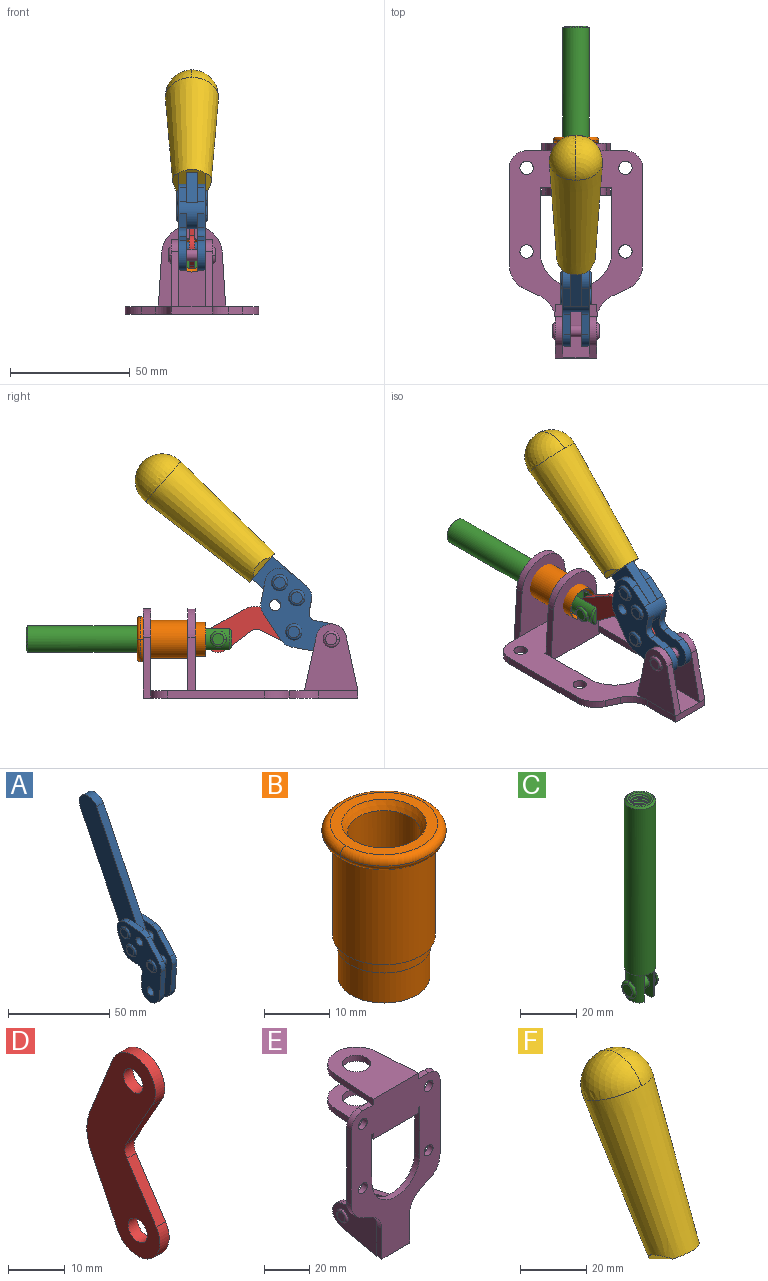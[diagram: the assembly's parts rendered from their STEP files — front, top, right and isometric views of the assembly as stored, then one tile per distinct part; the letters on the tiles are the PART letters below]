
ASSEMBLY  parts=6 mates=6
PART A: 59 faces, bbox 12.9x60.2x99.6 mm
  f0: torus R=2.39mm, axis (-1,0,0), area 14.9mm2, adj f20,f43,f51
  f1: torus R=2.39mm, axis (-1,0,0), area 14.9mm2, adj f19,f42,f51
  f2: torus R=2.39mm, axis (-1,0,0), area 14.9mm2, adj f18,f35,f51
  f3: torus R=2.39mm, axis (-1,0,0), area 14.9mm2, adj f14,f17,f23
  f4: torus R=2.39mm, axis (-1,0,0), area 14.9mm2, adj f13,f16,f23
  f5: torus R=2.39mm, axis (-1,0,0), area 14.9mm2, adj f12,f15,f23
  f6: cylinder r=2.39mm len=4.78mm, axis (1,0,0), area 46.5mm2, adj f48,f50,f51
  f7: cylinder r=2.39mm len=4.78mm, axis (1,0,0), area 46.5mm2, adj f50,f51
  f8: cylinder r=6.35mm len=12.68mm, axis (1,0,0), area 61.8mm2, adj f38,f39,f50,f51
  f9: cylinder r=2.39mm len=4.78mm, axis (-1,0,0), area 70.5mm2, adj f46,f50
  f10: cylinder r=2.39mm len=4.78mm, axis (-1,0,0), area 46.5mm2, adj f23,f45,f46
  f11: cylinder r=2.39mm len=4.78mm, axis (-1,0,0), area 46.5mm2, adj f23,f46
  f12: plane 4.78x4.78mm, normal (1,0,0), area 17.9mm2, adj f5,f15
  f13: plane 4.78x4.78mm, normal (1,0,0), area 17.9mm2, adj f4,f16
  f14: plane 4.78x4.78mm, normal (1,0,0), area 17.9mm2, adj f3,f17
  f15: torus R=2.39mm, axis (-1,0,0), area 14.9mm2, adj f5,f12,f23
  f16: torus R=2.39mm, axis (-1,0,0), area 14.9mm2, adj f4,f13,f23
  f17: torus R=2.39mm, axis (-1,0,0), area 14.9mm2, adj f3,f14,f23
  f18: plane 4.78x4.78mm, normal (-1,0,0), area 17.9mm2, adj f2,f35
  f19: plane 4.78x4.78mm, normal (-1,0,0), area 17.9mm2, adj f1,f42
  f20: plane 4.78x4.78mm, normal (-1,0,0), area 17.9mm2, adj f0,f43
  f21: plane 2.26x0.2mm, normal (1,0,0), area 0.2mm2, adj f31,f44
  f22: plane 2.26x0.2mm, normal (-1,0,0), area 0.2mm2, adj f41,f44
  f23: plane 39.37x30.77mm, normal (1,0,0), area 565.5mm2, adj f3,f4,f5,f10,f11,f15,f16,f17
  f24: cylinder r=6.1mm len=4.15mm, axis (-1,0,0), area 14.7mm2, adj f23,f25,f32,f46
  f25: plane 10.25x9.01mm, normal (0,-0.75,0.66), area 42.3mm2, adj f23,f24,f26,f46
  f26: cylinder r=6.35mm len=4.64mm, axis (-1,0,0), area 15.6mm2, adj f23,f25,f27,f46
  f27: plane 15.84x3.1mm, normal (0,-1,-0.07), area 49.2mm2, adj f23,f26,f28,f46
  f28: cylinder r=6.35mm len=12.68mm, axis (-1,0,0), area 61.8mm2, adj f23,f27,f29,f46
  f29: plane 8.11x3.1mm, normal (0,1,0.07), area 25.2mm2, adj f23,f28,f30,f46
  f30: cylinder r=3.05mm len=3.25mm, axis (-1,0,0), area 14.8mm2, adj f23,f29,f31,f46
  f31: plane 5.99x3.1mm, normal (0,0.07,-1), area 18.6mm2, adj f21,f23,f30,f44,f46
  f32: plane 9.5x3.1mm, normal (0,-0.07,1), area 29.5mm2, adj f23,f24,f33,f46,f47
  f33: cylinder r=6.1mm len=8.63mm, axis (-1,0,0), area 39.1mm2, adj f23,f32,f34,f47
  f34: plane 8.65x3.96mm, normal (0,0.91,-0.42), area 29.5mm2, adj f23,f33,f44,f47
  f35: torus R=2.39mm, axis (-1,0,0), area 14.9mm2, adj f2,f18,f51
  f36: plane 10.25x9.01mm, normal (0,-0.75,0.66), area 42.3mm2, adj f37,f49,f50,f51
  f37: cylinder r=6.35mm len=4.64mm, axis (1,0,0), area 15.6mm2, adj f36,f38,f50,f51
  f38: plane 15.84x3.1mm, normal (0,-1,-0.07), area 49.2mm2, adj f8,f37,f50,f51
  f39: plane 8.11x3.1mm, normal (0,1,0.07), area 25.2mm2, adj f8,f40,f50,f51
  f40: cylinder r=3.05mm len=3.25mm, axis (1,0,0), area 14.8mm2, adj f39,f41,f50,f51
  f41: plane 5.99x3.1mm, normal (0,0.07,-1), area 18.6mm2, adj f22,f40,f44,f50,f51
  f42: torus R=2.39mm, axis (-1,0,0), area 14.9mm2, adj f1,f19,f51
  f43: torus R=2.39mm, axis (-1,0,0), area 14.9mm2, adj f0,f20,f51
  f44: cylinder r=6.35mm len=12.12mm, axis (-1,0,0), area 128.9mm2, adj f21,f22,f23,f31,f34,f41,f46,f47
  f45: plane 2.65x1.35mm, normal (1,0,0), area 1mm2, adj f10,f55
  f46: plane 39.08x20.42mm, normal (-1,0,0), area 412.5mm2, adj f9,f10,f11,f24,f25,f26,f27,f28
  f47: plane 77.62x39.82mm, normal (1,0,0), area 850mm2, adj f32,f33,f34,f44,f53,f54,f55
  f48: plane 2.65x1.35mm, normal (-1,0,0), area 1mm2, adj f6,f55
  f49: cylinder r=6.1mm len=4.15mm, axis (1,0,0), area 14.7mm2, adj f36,f50,f51,f56
  f50: plane 39.08x20.42mm, normal (1,0,0), area 412.5mm2, adj f6,f7,f8,f9,f36,f37,f38,f39
  f51: plane 39.37x30.77mm, normal (-1,0,0), area 565.5mm2, adj f0,f1,f2,f6,f7,f8,f35,f36
  f52: plane 8.65x3.96mm, normal (0,0.91,-0.42), area 29.5mm2, adj f44,f51,f57,f58
  f53: plane 68.49x33.4mm, normal (0,0.9,-0.44), area 358.1mm2, adj f44,f47,f54,f58
  f54: cylinder r=6.35mm len=12.06mm, axis (1,0,0), area 93.7mm2, adj f47,f53,f55,f58
  f55: plane 68.49x33.4mm, normal (0,-0.9,0.44), area 358.1mm2, adj f44,f45,f46,f47,f48,f50,f54,f58
  f56: plane 9.5x3.1mm, normal (0,-0.07,1), area 29.5mm2, adj f49,f50,f51,f57,f58
  f57: cylinder r=6.1mm len=8.63mm, axis (1,0,0), area 39.1mm2, adj f51,f52,f56,f58
  f58: plane 77.62x39.82mm, normal (-1,0,0), area 850mm2, adj f44,f52,f53,f54,f55,f56,f57
PART B: 15 faces, bbox 20.6x20.6x28.7 mm
  f0: torus R=8.26mm, axis (0,0,1), area 56.8mm2, adj f1,f10,f12
  f1: torus R=8.26mm, axis (0,0,1), area 56.8mm2, adj f0,f6,f13
  f2: cylinder r=5.59mm len=25.91mm, axis (0,0,1), area 909.6mm2, adj f3,f4
  f3: cone r=6.86mm half-angle=45deg, axis (0,0,-1), area 70.2mm2, adj f2,f14
  f4: cone r=6.47mm half-angle=30deg, axis (0,0,1), area 66.7mm2, adj f2,f13
  f5: cylinder r=7.04mm len=14.07mm, axis (0,0,1), area 252.6mm2, adj f11,f14
  f6: torus R=8.26mm, axis (0,0,1), area 56.8mm2, adj f1,f12,f13
  f7: cylinder r=7.16mm len=14.33mm, axis (0,0,1), area 91.5mm2, adj f9,f11
  f8: cylinder r=7.86mm len=18.42mm, axis (0,0,1), area 909.6mm2, adj f9,f10
  f9: plane 15.72x15.72mm, normal (0,0,-1), area 33mm2, adj f7,f8
  f10: plane 16.51x16.51mm, normal (0,0,-1), area 19.9mm2, adj f0,f8,f12
  f11: plane 14.33x14.33mm, normal (0,0,-1), area 5.7mm2, adj f5,f7
  f12: torus R=8.26mm, axis (0,0,1), area 56.8mm2, adj f0,f6,f10
  f13: plane 16.51x16.51mm, normal (0,0,1), area 82.7mm2, adj f1,f4,f6
  f14: plane 14.07x14.07mm, normal (0,0,-1), area 7.8mm2, adj f3,f5
PART C: 48 faces, bbox 12.6x11.1x86.1 mm
  f0: torus R=2.41mm, axis (-1,0,0), area 15mm2, adj f30,f32,f34
  f1: torus R=2.41mm, axis (-1,0,0), area 15mm2, adj f29,f31,f33
  f2: cylinder r=5.54mm len=72.39mm, axis (0,0,1), area 2518.5mm2, adj f3,f4,f42,f43
  f3: cone r=5.54mm half-angle=45deg, axis (0,0,1), area 7.6mm2, adj f2,f5,f41
  f4: cone r=5.54mm half-angle=45deg, axis (0,0,-1), area 34.9mm2, adj f2,f39
  f5: cylinder r=5.08mm len=11.48mm, axis (0,0,1), area 108.3mm2, adj f3,f7,f8,f41
  f6: cylinder r=2.41mm len=4.83mm, axis (-1,0,0), area 71.2mm2, adj f40,f41
  f7: cylinder r=2.41mm len=4.83mm, axis (-1,0,0), area 7.6mm2, adj f5,f34
  f8: cone r=5.08mm half-angle=45deg, axis (0,0,1), area 10.6mm2, adj f5,f37,f41
  f9: cone r=3.98mm half-angle=45deg, axis (0,0,1), area 17.6mm2, adj f27,f39,f45,f46,f47
  f10: cylinder r=2.41mm len=4.83mm, axis (-1,0,0), area 7.6mm2, adj f33,f38
  f11: cylinder r=3.2mm len=6.4mm, axis (0,0,1), area 78.4mm2, adj f12,f28,f44,f45,f47
  f12: cylinder r=3.2mm len=6.4mm, axis (0,0,1), area 10.5mm2, adj f11,f13,f45,f47
  f13: cylinder r=3.2mm len=6.4mm, axis (0,0,1), area 10.5mm2, adj f12,f14,f45,f47
  f14: cylinder r=3.2mm len=6.4mm, axis (0,0,1), area 10.5mm2, adj f13,f15,f45,f47
  f15: cylinder r=3.2mm len=6.4mm, axis (0,0,1), area 10.5mm2, adj f14,f16,f45,f47
  f16: cylinder r=3.2mm len=6.4mm, axis (0,0,1), area 10.5mm2, adj f15,f17,f45,f47
  f17: cylinder r=3.2mm len=6.4mm, axis (0,0,1), area 10.5mm2, adj f16,f18,f45,f47
  f18: cylinder r=3.2mm len=6.4mm, axis (0,0,1), area 10.5mm2, adj f17,f19,f45,f47
  f19: cylinder r=3.2mm len=6.4mm, axis (0,0,1), area 10.5mm2, adj f18,f20,f45,f47
  f20: cylinder r=3.2mm len=6.4mm, axis (0,0,1), area 10.5mm2, adj f19,f21,f45,f47
  f21: cylinder r=3.2mm len=6.4mm, axis (0,0,1), area 10.5mm2, adj f20,f22,f45,f47
  f22: cylinder r=3.2mm len=6.4mm, axis (0,0,1), area 10.5mm2, adj f21,f23,f45,f47
  f23: cylinder r=3.2mm len=6.4mm, axis (0,0,1), area 10.5mm2, adj f22,f24,f45,f47
  f24: cylinder r=3.2mm len=6.4mm, axis (0,0,1), area 10.5mm2, adj f23,f25,f45,f47
  f25: cylinder r=3.2mm len=6.4mm, axis (0,0,1), area 10.5mm2, adj f24,f26,f45,f47
  f26: cylinder r=3.2mm len=6.4mm, axis (0,0,1), area 10.5mm2, adj f25,f27,f45,f47
  f27: cylinder r=3.2mm len=6.4mm, axis (0,0,1), area 7.4mm2, adj f9,f26,f45,f47
  f28: cone r=3.2mm half-angle=60deg, axis (0,0,1), area 37.2mm2, adj f11
  f29: plane 4.83x4.83mm, normal (-1,0,0), area 18.3mm2, adj f1,f31
  f30: plane 4.83x4.83mm, normal (1,0,0), area 18.3mm2, adj f0,f32
  f31: torus R=2.41mm, axis (-1,0,0), area 15mm2, adj f1,f29,f33
  f32: torus R=2.41mm, axis (-1,0,0), area 15mm2, adj f0,f30,f34
  f33: plane 6.83x6.83mm, normal (1,0,0), area 18.3mm2, adj f1,f10,f31
  f34: plane 6.83x6.83mm, normal (-1,0,0), area 18.3mm2, adj f0,f7,f32
  f35: cone r=5.08mm half-angle=45deg, axis (0,0,1), area 10.6mm2, adj f36,f38,f40
  f36: plane 7.25x1.97mm, normal (0,0,-1), area 10mm2, adj f35,f40
  f37: plane 7.25x1.97mm, normal (0,0,-1), area 10mm2, adj f8,f41
  f38: cylinder r=5.08mm len=11.48mm, axis (0,0,1), area 108.3mm2, adj f10,f35,f40,f42
  f39: plane 9.55x9.55mm, normal (0,0,1), area 22mm2, adj f4,f9
  f40: plane 12.76x10.09mm, normal (1,0,0), area 95.7mm2, adj f6,f35,f36,f38,f42,f43
  f41: plane 12.76x10.09mm, normal (-1,0,0), area 95.7mm2, adj f3,f5,f6,f8,f37,f43
  f42: cone r=5.54mm half-angle=45deg, axis (0,0,1), area 7.6mm2, adj f2,f38,f40
  f43: plane 11.07x4.7mm, normal (0,0,-1), area 50.4mm2, adj f2,f40,f41
  f44: plane 0.89x0.62mm, normal (-1,0,0), area 0.3mm2, adj f11,f45,f46,f47
  f45: bspline ~24.8x7.63mm, area 266.6mm2, adj f9,f11,f12,f13,f14,f15,f16,f17
  f46: bspline ~24.87x7.63mm, area 73.6mm2, adj f9,f44,f45,f47
  f47: bspline ~24.98x7.63mm, area 272.5mm2, adj f9,f11,f12,f13,f14,f15,f16,f17
PART D: 12 faces, bbox 2.3x18.2x42.8 mm
  f0: cylinder r=2.4mm len=4.8mm, axis (1,0,0), area 34.9mm2, adj f4,f11
  f1: cylinder r=10.41mm len=8.47mm, axis (1,0,0), area 20.2mm2, adj f4,f9,f10,f11
  f2: cylinder r=3.05mm len=3.16mm, axis (1,0,0), area 7.7mm2, adj f4,f6,f7,f11
  f3: cylinder r=2.4mm len=4.8mm, axis (1,0,0), area 34.9mm2, adj f4,f11
  f4: plane 42.81x18.23mm, normal (-1,0,0), area 414.1mm2, adj f0,f1,f2,f3,f5,f6,f7,f8
  f5: cylinder r=5.54mm len=10.67mm, axis (1,0,0), area 41.8mm2, adj f4,f6,f10,f11
  f6: plane 11.66x6.53mm, normal (0,-0.87,-0.49), area 30.9mm2, adj f2,f4,f5,f11
  f7: plane 11.17x7.33mm, normal (0,-0.84,0.55), area 30.9mm2, adj f2,f4,f8,f11
  f8: cylinder r=5.54mm len=10.51mm, axis (1,0,0), area 41.8mm2, adj f4,f7,f9,f11
  f9: plane 13.67x6.67mm, normal (0,0.9,-0.44), area 35.1mm2, adj f1,f4,f8,f11
  f10: plane 14.1x5.7mm, normal (0,0.93,0.37), area 35.1mm2, adj f1,f4,f5,f11
  f11: plane 42.81x18.23mm, normal (1,0,0), area 414.1mm2, adj f0,f1,f2,f3,f5,f6,f7,f8
PART E: 55 faces, bbox 55.7x37.4x89.8 mm
  f0: torus R=2.41mm, axis (-1,0,0), area 15mm2, adj f11,f15,f25
  f1: torus R=2.41mm, axis (-1,0,0), area 15mm2, adj f10,f12,f22
  f2: cylinder r=2.78mm len=5.56mm, axis (0,-1,0), area 54.2mm2, adj f30,f54
  f3: cylinder r=14.99mm len=29.97mm, axis (0,-1,0), area 145.9mm2, adj f30,f49,f53,f54
  f4: cylinder r=2.78mm len=5.56mm, axis (0,-1,0), area 54.2mm2, adj f30,f54
  f5: cylinder r=2.78mm len=5.56mm, axis (0,-1,0), area 54.2mm2, adj f30,f54
  f6: cylinder r=2.78mm len=5.56mm, axis (0,-1,0), area 54.2mm2, adj f30,f54
  f7: cylinder r=6.35mm len=12.7mm, axis (0,0,1), area 123.6mm2, adj f27,f51
  f8: cylinder r=6.35mm len=12.7mm, axis (0,0,-1), area 124.7mm2, adj f21,f35
  f9: cylinder r=2.41mm len=11.18mm, axis (-1,0,0), area 169.4mm2, adj f16,f19
  f10: plane 4.83x4.83mm, normal (1,0,0), area 18.3mm2, adj f1,f12
  f11: plane 4.83x4.83mm, normal (-1,0,0), area 18.3mm2, adj f0,f15
  f12: torus R=2.41mm, axis (-1,0,0), area 15mm2, adj f1,f10,f22
  f13: cylinder r=6.35mm len=12.41mm, axis (1,0,0), area 53.4mm2, adj f18,f19,f22,f23
  f14: cylinder r=6.35mm len=12.41mm, axis (-1,0,0), area 53.4mm2, adj f16,f17,f24,f25
  f15: torus R=2.41mm, axis (-1,0,0), area 15mm2, adj f0,f11,f25
  f16: plane 27.86x22.35mm, normal (1,0,0), area 425.4mm2, adj f9,f14,f17,f24,f30
  f17: plane 22.86x4.97mm, normal (0,0.21,0.98), area 72.5mm2, adj f14,f16,f25,f30
  f18: plane 22.86x4.97mm, normal (0,0.21,0.98), area 72.5mm2, adj f13,f19,f22,f30
  f19: plane 27.86x22.35mm, normal (-1,0,0), area 425.4mm2, adj f9,f13,f18,f23,f30
  f20: cylinder r=12.7mm len=25.35mm, axis (0,0,-1), area 119.8mm2, adj f21,f34,f35,f36
  f21: plane 34.21x28.07mm, normal (0,0,-1), area 702.4mm2, adj f8,f20,f30,f34,f36
  f22: plane 27.96x22.45mm, normal (1,0,0), area 407.2mm2, adj f1,f12,f13,f18,f23,f30,f42,f43
  f23: plane 22.86x4.97mm, normal (0,0.21,-0.98), area 72.5mm2, adj f13,f19,f22,f44
  f24: plane 22.86x4.97mm, normal (0,0.21,-0.98), area 72.5mm2, adj f14,f16,f25,f44
  f25: plane 27.86x22.35mm, normal (-1,0,0), area 407.1mm2, adj f0,f14,f15,f17,f24,f30,f45,f46
  f26: plane 3.1x0.95mm, normal (0,0,-1), area 2.7mm2, adj f30,f49,f50,f54
  f27: plane 34.21x28.07mm, normal (0,0,1), area 702.4mm2, adj f7,f28,f30,f50,f52
  f28: cylinder r=12.7mm len=25.35mm, axis (0,0,1), area 118.8mm2, adj f27,f50,f51,f52
  f29: plane 3.1x0.95mm, normal (0,0,-1), area 2.7mm2, adj f30,f52,f53,f54
  f30: plane 86.54x55.63mm, normal (0,1,0), area 2362.9mm2, adj f2,f3,f4,f5,f6,f16,f17,f18
  f31: plane 40.56x3.1mm, normal (-1,0,0), area 125.7mm2, adj f30,f32,f48,f54
  f32: cylinder r=7.11mm len=7.11mm, axis (0,-1,0), area 34.6mm2, adj f30,f31,f33,f54
  f33: plane 6.67x3.1mm, normal (0,0,1), area 20.4mm2, adj f30,f32,f34,f54
  f34: plane 25.39x3.13mm, normal (-1,0.06,0), area 79.5mm2, adj f20,f21,f33,f35,f54
  f35: plane 37.31x28.45mm, normal (0,0,1), area 789.9mm2, adj f8,f20,f34,f36,f54
  f36: plane 25.39x3.13mm, normal (1,0.06,0), area 79.5mm2, adj f20,f21,f35,f37,f54
  f37: plane 6.67x3.1mm, normal (0,0,1), area 20.4mm2, adj f30,f36,f38,f54
  f38: cylinder r=7.11mm len=7.11mm, axis (0,-1,0), area 34.6mm2, adj f30,f37,f39,f54
  f39: plane 40.56x3.1mm, normal (1,0,0), area 125.7mm2, adj f30,f38,f40,f54
  f40: cylinder r=11.18mm len=10.16mm, axis (0,-1,0), area 39.5mm2, adj f30,f39,f41,f54
  f41: plane 6.09x3.1mm, normal (0.42,0,-0.91), area 20.8mm2, adj f30,f40,f42,f54
  f42: cylinder r=11.18mm len=9.41mm, axis (0,-1,0), area 37.2mm2, adj f22,f30,f41,f43,f54
  f43: plane 16.5x3.1mm, normal (1,0,0), area 51.1mm2, adj f22,f42,f44,f54
  f44: plane 17.37x3.1mm, normal (0,0,-1), area 53.8mm2, adj f23,f24,f30,f43,f45,f54
  f45: plane 16.5x3.1mm, normal (-1,0,0), area 51.1mm2, adj f25,f44,f46,f54
  f46: cylinder r=11.18mm len=9.41mm, axis (0,-1,0), area 37.2mm2, adj f25,f30,f45,f47,f54
  f47: plane 6.09x3.1mm, normal (-0.42,0,-0.91), area 20.8mm2, adj f30,f46,f48,f54
  f48: cylinder r=11.18mm len=10.16mm, axis (0,-1,0), area 39.5mm2, adj f30,f31,f47,f54
  f49: plane 26.54x3.1mm, normal (-1,0,0), area 82.3mm2, adj f3,f26,f30,f54
  f50: plane 25.39x3.1mm, normal (1,0.06,0), area 78.8mm2, adj f26,f27,f28,f51,f54
  f51: plane 37.31x28.45mm, normal (0,0,-1), area 789.9mm2, adj f7,f28,f50,f52,f54
  f52: plane 25.39x3.1mm, normal (-1,0.06,0), area 78.8mm2, adj f27,f28,f29,f51,f54
  f53: plane 26.54x3.1mm, normal (1,0,0), area 82.3mm2, adj f3,f29,f30,f54
  f54: plane 89.66x55.63mm, normal (0,-1,0), area 2678.5mm2, adj f2,f3,f4,f5,f6,f26,f29,f31
PART F: 11 faces, bbox 22.3x42.6x64.5 mm
  f0: sphere r=11.13mm, area 411.4mm2, adj f1,f8
  f1: cone r=11.11mm half-angle=3.3deg, axis (0,0.44,0.9), area 3251.8mm2, adj f0,f7,f8,f9,f10
  f2: cylinder r=6.16mm len=11.7mm, axis (1,0,0), area 89.5mm2, adj f3,f4,f5,f6
  f3: plane 60.23x36.75mm, normal (-1,0,0), area 763.6mm2, adj f2,f4,f6,f10
  f4: plane 51.37x25.05mm, normal (0,0.9,-0.44), area 264.2mm2, adj f2,f3,f5,f10
  f5: plane 60.23x36.75mm, normal (1,0,0), area 763.6mm2, adj f2,f4,f6,f10
  f6: plane 51.37x25.05mm, normal (0,-0.9,0.44), area 264.2mm2, adj f2,f3,f5,f10
  f7: plane 9.95x5.95mm, normal (0.71,-0.31,-0.64), area 25.8mm2, adj f1,f10
  f8: sphere r=11.13mm, area 411.4mm2, adj f0,f1
  f9: plane 9.95x5.95mm, normal (-0.71,-0.31,-0.64), area 25.8mm2, adj f1,f10
  f10: plane 14.27x11.38mm, normal (0,-0.44,-0.9), area 106.7mm2, adj f1,f3,f4,f5,f6,f7,f9
PLACE A rot(axis=(0,-0.61,-0.79),180deg) t=(0,-3.86,9.14)mm
PLACE B rot(axis=(-1,0,0),90deg) t=(0,-9.14,49.23)mm
PLACE C rot(axis=(-1,0,0),90deg) t=(0,-9.52,49.23)mm
PLACE D rot(axis=(1,0,0),86.5deg) t=(0,-11.7,2.14)mm
PLACE E rot(axis=(0,-0.71,-0.71),180deg) t=(0,-9.14,0)mm fixed
PLACE F rot(axis=(0,0.61,0.79),180deg) t=(-0.04,-3.86,9.14)mm
MATE fastened F.f2 <-> A.f54  axis (1,0,0) through (-2.35,30.66,91.94)mm
MATE revolute D.f5 <-> A.f4  axis (1,0,0) through (0,-25.65,27.64)mm
MATE fastened B.f2 <-> E.f7  axis (0,1,0) through (0,37.25,24.61)mm
MATE revolute A.f7 <-> E.f0  axis (-1,0,0) through (0,-41.23,24.61)mm
MATE revolute D.f3 <-> C.f6  axis (1,0,0) through (0,5.96,24.61)mm
MATE slider B.f12 <-> C.f2  axis (0,1,0) through (0,39.79,24.61)mm
